# Revit family: RSJ-15-185RDN7-L1
name_source: partatom
category: Mechanical Equipment
revit_build: Autodesk Revit 2013 (Build: 20120221_2030(x64)
units: mm (PartAtom-declared; Revit-internal decimal feet)

## types (1)
- RSJ-15/185RDN7-L1
    Air  Flow = 350 m3/h
    Description = Heat Pump Water
    Drain pipe = 20 mm  [stored 0.0656168 ft]
    Gas = R290
    Heat pump Water heating Capacity = 0 W
    Height = 1730 mm  [stored 5.67585 ft]
    Installation = Unit installation
    Length = 560 mm  [stored 1.83727 ft]
    Machine material = Galvanized Steel
    Max. current = 0 A
    Maximum Fuse Amps = 0 A
    Model = RSJ-15/185RDN7-L1
    Net Weight = 91.00 kg
    PTR valve joint = 0 mm  [stored 0 ft]
    Panel color = Polar white
    Power supply = 1 phase, 220-240V, 50Hz
    Series = Combo
    Storage size = 185.0 L
    Water inlet pipe = 20 mm  [stored 0.0656168 ft]
    Water outlet pipe = 20 mm  [stored 0.0656168 ft]
    Width = 595 mm  [stored 1.9521 ft]
    clearance access left = 0 mm  [stored 0 ft]
    clearance access right = 0 mm  [stored 0 ft]
    clearance access up = 0 mm  [stored 0 ft]

note: [stored X ft] marks values corroborated as IEEE doubles in the binary element streams (Revit-internal decimal feet)

## geometry (parser evidence)
native form markers: Sweep x2
no freeform markers — native parametric forms only
